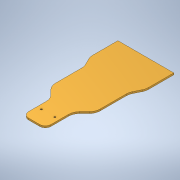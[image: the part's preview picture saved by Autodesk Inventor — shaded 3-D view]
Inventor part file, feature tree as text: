
AUTODESK INVENTOR PART (.ipt)
format: ipt  version: 2020 (Build 240168000, 168)  size: 164,352 bytes
history: native  units: mm
features: thread x2, sketch x2, extrude x1, plane x1, hole x1
ambient origin geometry x8: Origin, YZ Plane, XZ Plane, XY Plane, X Axis, Y Axis, Z Axis, Center Point
bodies: Body1 (feature_tree)
feature tree (7):
  extrude  "Extrusion2"  Depth=60.0mm
  plane  "Work Plane1"
  hole  "Hole2"  [1 undecoded]
  thread  "Thread1"  [1 undecoded]
  thread  "Thread2"  [1 undecoded]
  sketch  "Sketch1"  dims[d23=50.0mm d24=60.0mm]
  sketch  "Sketch8"  dims[d25=60.0mm d26=50.0mm d27=50.0mm d28=50.0mm d29=20.0mm d30=20.0mm d31=40.0mm d32=100.0mm d34=10.0mm d35=10.0mm d36=20.0mm d37=200.0mm d38=20.0mm d39=10.0mm d40=3.0mm d41=0.0mm d42=-25.0mm d61=15.0mm d106=3.0mm d107=6.0mm d108=4.0mm d109=2.0mm d110=90.0deg d111=8.0mm d112=20.594885mm d113=3.0mm d114=0.0mm d115=3.0mm d116=0.0mm d117=8.0mm d118=8.0mm d119=25.0mm d120=25.0mm d57=0.5mm d58=0.872665mm d59=0.5mm d60=0.872665mm]
note: 3 required parameter values undecoded (feature->parameter linkage not recoverable at this tier; creation-order binding heuristic only, values carry confidence <= 0.55)
